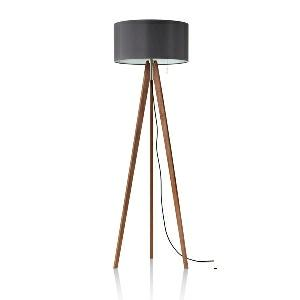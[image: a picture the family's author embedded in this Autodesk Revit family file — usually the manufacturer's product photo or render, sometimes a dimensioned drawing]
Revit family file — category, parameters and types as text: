
# Revit family: vivaa_free_-_vfs_7000_940_d_00812669_fbbb
name_source: partatom
category: Lighting Fixtures
units: mm (PartAtom-declared; Revit-internal decimal feet)

## family parameters
Cut with Voids When Loaded = No
Host = Face
Light Source = No
Part Type = Normal
Room Calculation Point = No
Round Connector Dimension = Use Diameter
Shared = No

## types (1)
- VIVAA.free - VFS 7000/940/D (1 x LED, 7200 lm, 4000K)
    Apparent Load = 79 VA
    Approval mark = CE
    CIE Flux Codes = 52 82 95 44 100
    Color Rendering = 90-100
    Color Temperature = 4000K
    Control Gear = Electronic ballast
    Default Elevation = 1800 mm
    Description = VFS 7000/940/D|Free-standing luminaire|light source:   Cold white   |work equipment: Electronic ballast|luminous flux: 7200 lm|light distribution: Direct/indirect|direct ratio: approx. 44 %|color rendering index (CRI): >= 90|chromaticity tolerance:  3 SDCM|technology: Continuously dimmable|operation: Pull cord|luminaire body|material: Polyethylene(PE)|surface: Untreated|colour: Anthracite|lamp cover: Polycarbonate (PC), Satine|tubular section|material: Wood|surface: Stained|Form: Tubular section upright|colour of tubular section: Ash dark|weight (net): approx. 6.4 kg|mains lead: 3.40 m Mains plug CEE 7/VII|Fastening: Floor standing base|glare control: Diffusor|luminance(L65): <= 1600 cd/m|unified glare rating(4H 8H): <=  16|
    Frequency = 50 Hz, 60 Hz
    Height = 250 mm
    Lamp = 1 x LED
    Lamp Light Flux = 7200 lm
    Lamp count = 1
    Length = 520 mm
    Luminous efficacy = 91 lm/W
    Manufacturer = Waldmann
    ModVariant = No
    Model = 00812669
    Mounting Place = Floor
    Mounting Type = Freestanding
    Number of Poles = 1
    OnlyDefault = Yes
    Power Factor = 1
    Product Name = VIVAA.free - VFS 7000/940/D
    Product group = Free standing luminaire
    ProductGroupID = 13
    Protection Class = Protection class I
    Protection Degree = Degree of protection
    RLX_Detail_Level = 1
    RLX_Emergency_Light_Flux = 0 lm
    RLX_Emergency_Type = 0
    RLX_Emergency_Type_DB = No
    RlxData = <blob elided: 29337 chars, md5=0e456cc8>
    Socket = socket
    Standby Power = 0 W
    System Light Flux = 7200 lm
    System Power = 79 W
    Type Comments = Product without accessories
    Type Image = vivaa_free_wood_rgb.jpg
    URL = http://relux.com
    VarID = ---
    Voltage = 230 V
    Voltage Range = 220-240 V
    Weight = 0.00 kg
    Width = 0 mm  [stored 0 ft]

note: [stored X ft] marks values corroborated as IEEE doubles in the binary element streams (Revit-internal decimal feet)

## geometry (parser evidence)
native form markers: Blend x4, Sweep x17
no freeform markers — native parametric forms only
